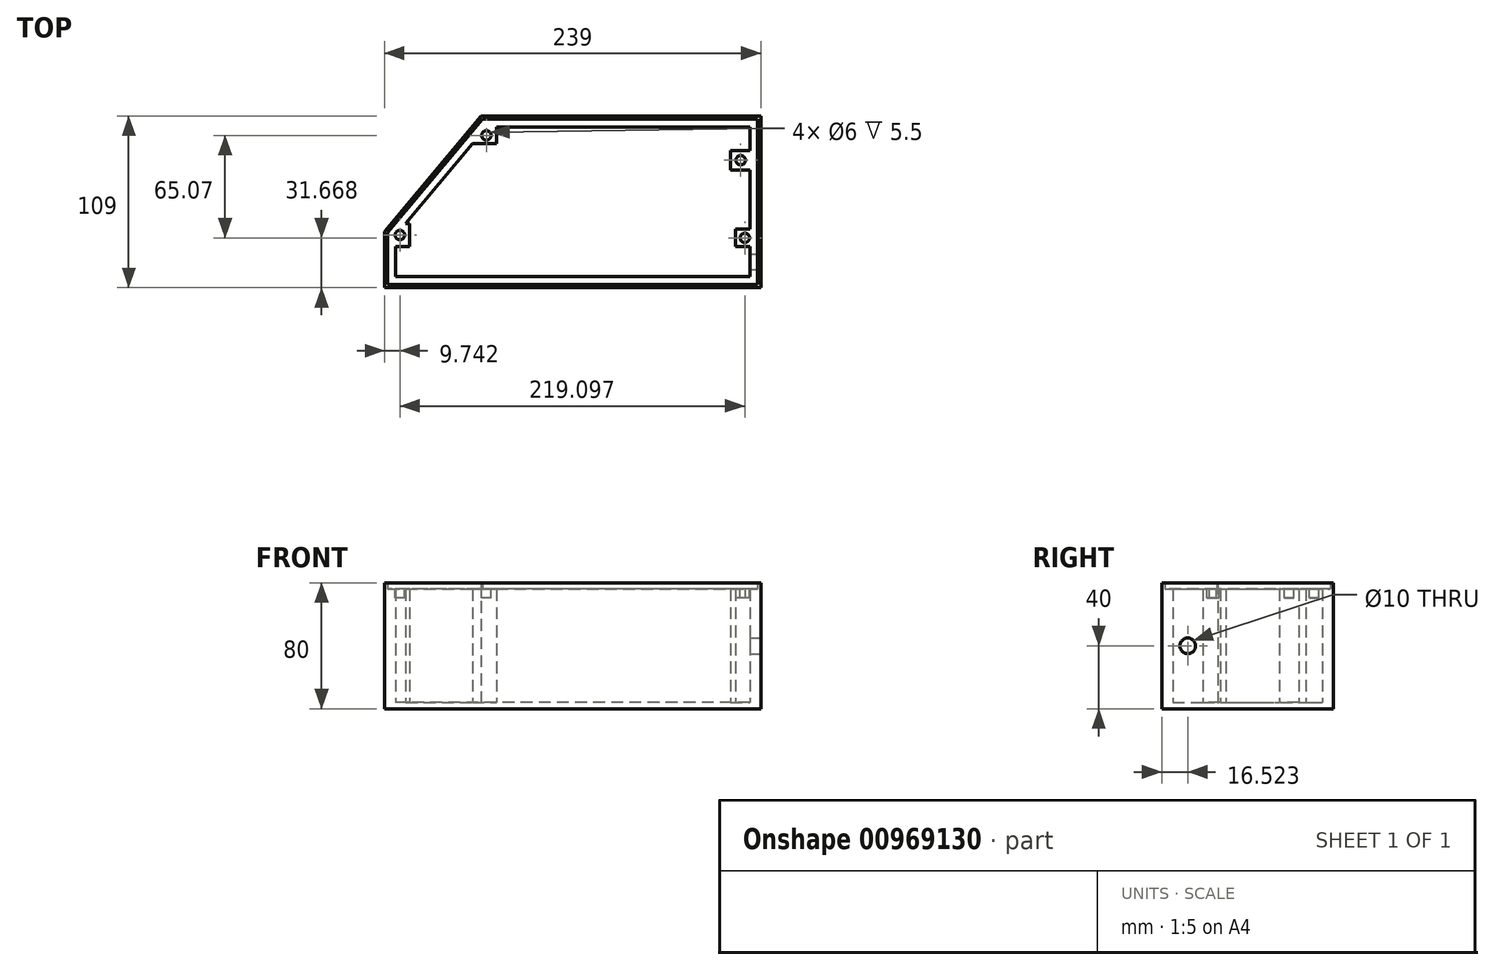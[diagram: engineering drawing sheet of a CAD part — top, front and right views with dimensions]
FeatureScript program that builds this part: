
annotation { "Feature Type Name" : "Feature", "Feature Type Description" : "" }
export const myFeature = defineFeature(function(context is Context, id is Id, definition is map)
    precondition{}
    {
        {
            var Q0;
            Q0=qCreatedBy(makeId("Top.planeOp"),FACE);
            var sketch = newSketch(context, id + "F0", { "sketchPlane" : qUnion([Q0])});
            skLineSegment(sketch, "E0", {"start": v(0, 0) * mm, "end": v(-225, 0) * mm});
            skLineSegment(sketch, "E1", {"start": v(0, 0) * mm, "end": v(0, 19.05) * mm});
            skLineSegment(sketch, "E2", {"start": v(-225, 0) * mm, "end": v(-225, 19) * mm});
            skLineSegment(sketch, "E3", {"start": v(-218.6, 33.87) * mm, "end": v(-176.22, 84.48) * mm});
            skLineSegment(sketch, "E4.0", {"start": v(0, 9) * mm, "end": v(-280, 9) * mm});
            skCircle(sketch, "E5", {"center": v(-29.7, 70.77) * mm, "radius": 9 * mm});
            skCircle(sketch, "E6.1.0.0", {"center": v(-214.7, 9) * mm, "radius": 9 * mm});
            skCircle(sketch, "E6.2.0.0", {"center": v(-196.2, 9) * mm, "radius": 9 * mm});
            skCircle(sketch, "E6.3.0.0", {"center": v(-177.7, 9) * mm, "radius": 9 * mm});
            skCircle(sketch, "E6.4.0.0", {"center": v(-159.2, 9) * mm, "radius": 9 * mm});
            skCircle(sketch, "E6.5.0.0", {"center": v(-140.7, 9) * mm, "radius": 9 * mm});
            skCircle(sketch, "E6.6.0.0", {"center": v(-122.2, 9) * mm, "radius": 9 * mm});
            skCircle(sketch, "E6.7.0.0", {"center": v(-103.7, 9) * mm, "radius": 9 * mm});
            skCircle(sketch, "E6.8.0.0", {"center": v(-85.2, 9) * mm, "radius": 9 * mm});
            skCircle(sketch, "E6.9.0.0", {"center": v(-66.7, 9) * mm, "radius": 9 * mm});
            skCircle(sketch, "E6.10.0.0", {"center": v(-48.2, 9) * mm, "radius": 9 * mm});
            skCircle(sketch, "E6.11.0.0", {"center": v(-29.7, 9) * mm, "radius": 9 * mm});
            skCircle(sketch, "E6.12.0.0", {"center": v(-11.2, 9) * mm, "radius": 9 * mm});
            skLineSegment(sketch, "E6.direction1", {"start": v(-231, 9) * mm, "end": v(-212.5, 9) * mm, "construction": true});
            skCircle(sketch, "E7", {"center": v(-186.95, 55.32) * mm, "radius": 9 * mm});
            skCircle(sketch, "E8.1.0.0", {"center": v(-205.45, 24.44) * mm, "radius": 9 * mm});
            skCircle(sketch, "E8.2.0.0", {"center": v(-186.95, 24.44) * mm, "radius": 9 * mm});
            skCircle(sketch, "E8.3.0.0", {"center": v(-168.45, 24.44) * mm, "radius": 9 * mm});
            skCircle(sketch, "E8.4.0.0", {"center": v(-149.95, 24.44) * mm, "radius": 9 * mm});
            skCircle(sketch, "E8.5.0.0", {"center": v(-131.45, 24.44) * mm, "radius": 9 * mm});
            skCircle(sketch, "E8.6.0.0", {"center": v(-112.95, 24.44) * mm, "radius": 9 * mm});
            skCircle(sketch, "E8.7.0.0", {"center": v(-94.45, 24.44) * mm, "radius": 9 * mm});
            skCircle(sketch, "E8.8.0.0", {"center": v(-75.95, 24.44) * mm, "radius": 9 * mm});
            skCircle(sketch, "E8.9.0.0", {"center": v(-57.45, 24.44) * mm, "radius": 9 * mm});
            skCircle(sketch, "E8.10.0.0", {"center": v(-38.95, 24.44) * mm, "radius": 9 * mm});
            skCircle(sketch, "E8.11.0.0", {"center": v(-20.45, 24.44) * mm, "radius": 9 * mm});
            skLineSegment(sketch, "E8.direction1", {"start": v(-221.75, 24.44) * mm, "end": v(-203.25, 24.44) * mm, "construction": true});
            skCircle(sketch, "E9", {"center": v(-196.2, 39.88) * mm, "radius": 9 * mm});
            skCircle(sketch, "E10.1.0.0", {"center": v(-177.7, 39.88) * mm, "radius": 9 * mm});
            skCircle(sketch, "E10.2.0.0", {"center": v(-159.2, 39.88) * mm, "radius": 9 * mm});
            skCircle(sketch, "E10.3.0.0", {"center": v(-140.7, 39.88) * mm, "radius": 9 * mm});
            skCircle(sketch, "E10.4.0.0", {"center": v(-122.2, 39.88) * mm, "radius": 9 * mm});
            skCircle(sketch, "E10.5.0.0", {"center": v(-103.7, 39.88) * mm, "radius": 9 * mm});
            skCircle(sketch, "E10.6.0.0", {"center": v(-85.2, 39.88) * mm, "radius": 9 * mm});
            skCircle(sketch, "E10.7.0.0", {"center": v(-66.7, 39.88) * mm, "radius": 9 * mm});
            skCircle(sketch, "E10.8.0.0", {"center": v(-48.2, 39.88) * mm, "radius": 9 * mm});
            skCircle(sketch, "E10.9.0.0", {"center": v(-29.7, 39.88) * mm, "radius": 9 * mm});
            skCircle(sketch, "E10.10.0.0", {"center": v(-11.2, 39.88) * mm, "radius": 9 * mm});
            skLineSegment(sketch, "E10.direction1", {"start": v(-194, 39.88) * mm, "end": v(-175.5, 39.88) * mm, "construction": true});
            skCircle(sketch, "E11", {"center": v(-168.45, 55.32) * mm, "radius": 9 * mm});
            skCircle(sketch, "E12.1.0.0", {"center": v(-149.95, 55.32) * mm, "radius": 9 * mm});
            skCircle(sketch, "E12.2.0.0", {"center": v(-131.45, 55.32) * mm, "radius": 9 * mm});
            skCircle(sketch, "E12.3.0.0", {"center": v(-112.95, 55.32) * mm, "radius": 9 * mm});
            skCircle(sketch, "E12.4.0.0", {"center": v(-94.45, 55.32) * mm, "radius": 9 * mm});
            skCircle(sketch, "E12.5.0.0", {"center": v(-75.95, 55.32) * mm, "radius": 9 * mm});
            skCircle(sketch, "E12.6.0.0", {"center": v(-57.45, 55.32) * mm, "radius": 9 * mm});
            skCircle(sketch, "E12.7.0.0", {"center": v(-38.95, 55.32) * mm, "radius": 9 * mm});
            skCircle(sketch, "E12.8.0.0", {"center": v(-20.45, 55.32) * mm, "radius": 9 * mm});
            skLineSegment(sketch, "E12.direction1", {"start": v(-168.45, 55.32) * mm, "end": v(-149.95, 55.32) * mm, "construction": true});
            skLineSegment(sketch, "E13.0", {"start": v(0, 95) * mm, "end": v(-160.95, 95) * mm});
            skCircle(sketch, "E14", {"center": v(-159.2, 70.77) * mm, "radius": 9 * mm});
            skCircle(sketch, "E15.1.0.0", {"center": v(-140.7, 70.77) * mm, "radius": 9 * mm});
            skCircle(sketch, "E15.2.0.0", {"center": v(-122.2, 70.77) * mm, "radius": 9 * mm});
            skCircle(sketch, "E15.3.0.0", {"center": v(-103.7, 70.77) * mm, "radius": 9 * mm});
            skCircle(sketch, "E15.4.0.0", {"center": v(-85.2, 70.77) * mm, "radius": 9 * mm});
            skCircle(sketch, "E15.5.0.0", {"center": v(-66.7, 70.77) * mm, "radius": 9 * mm});
            skCircle(sketch, "E15.6.0.0", {"center": v(-48.2, 70.77) * mm, "radius": 9 * mm});
            skLineSegment(sketch, "E15.direction1", {"start": v(-159.2, 70.77) * mm, "end": v(-140.7, 70.77) * mm, "construction": true});
            skLineSegment(sketch, "E16.0", {"start": v(-232, 28.77) * mm, "end": v(-170.67, 102) * mm});
            skLineSegment(sketch, "E16.1", {"start": v(7, 102) * mm, "end": v(-170.67, 102) * mm});
            skLineSegment(sketch, "E16.2", {"start": v(7, -7) * mm, "end": v(7, 102) * mm});
            skLineSegment(sketch, "E17.0", {"start": v(-232, -7) * mm, "end": v(-232, 28.77) * mm});
            skLineSegment(sketch, "E18.0", {"start": v(7, -7) * mm, "end": v(-232, -7) * mm});
            skLineSegment(sketch, "E19", {"start": v(-218.6, 33.87) * mm, "end": v(-216.07, 33.87) * mm});
            skLineSegment(sketch, "E20", {"start": v(-216.07, 19) * mm, "end": v(-225, 19) * mm});
            skLineSegment(sketch, "E21", {"start": v(-216.07, 19) * mm, "end": v(-216.07, 33.87) * mm});
            skLineSegment(sketch, "E22", {"start": v(0, 30.29) * mm, "end": v(-9.02, 30.29) * mm});
            skLineSegment(sketch, "E23", {"start": v(-9.02, 30.29) * mm, "end": v(-9.02, 19.05) * mm});
            skLineSegment(sketch, "E24", {"start": v(-9.02, 19.05) * mm, "end": v(0, 19.05) * mm});
            skLineSegment(sketch, "E25.trimOffspring", {"start": v(0, 30.29) * mm, "end": v(0, 67.76) * mm});
            skLineSegment(sketch, "E26", {"start": v(-176.22, 84.48) * mm, "end": v(-160.95, 84.48) * mm});
            skLineSegment(sketch, "E27", {"start": v(-160.95, 84.48) * mm, "end": v(-160.95, 95) * mm});
            skLineSegment(sketch, "E28", {"start": v(0, 80.25) * mm, "end": v(-12.43, 80.2) * mm});
            skLineSegment(sketch, "E29", {"start": v(-12.43, 80.2) * mm, "end": v(-12.38, 67.76) * mm});
            skLineSegment(sketch, "E30", {"start": v(-12.38, 67.76) * mm, "end": v(0, 67.76) * mm});
            skLineSegment(sketch, "E31.trimOffspring", {"start": v(0, 80.25) * mm, "end": v(0, 95) * mm});
            skSolve(sketch);
        }
        {
            var Q0;
            Q0 = qSketchRegion(id + "F0", true);
            extrude(context, id + "F1", {"entities" : qUnion([Q0]), "depth" : 72 * mm, "offsetDistance" : 25 * mm});
        }
        {
            var Q0;
            Q0=qCreatedBy(makeId("Top.planeOp"),FACE);
            var sketch = newSketch(context, id + "F2", { "sketchPlane" : qUnion([Q0])});
            skLineSegment(sketch, "E32.0.0", {"start": v(-232, 28.77) * mm, "end": v(-170.67, 102) * mm});
            skLineSegment(sketch, "E32.0.1", {"start": v(-170.67, 102) * mm, "end": v(7, 102) * mm});
            skLineSegment(sketch, "E32.0.2", {"start": v(7, 102) * mm, "end": v(7, -7) * mm});
            skLineSegment(sketch, "E32.0.3", {"start": v(7, -7) * mm, "end": v(-232, -7) * mm});
            skLineSegment(sketch, "E32.0.4", {"start": v(-232, -7) * mm, "end": v(-232, 28.77) * mm});
            skSolve(sketch);
        }
        {
            var Q0;
            Q0 = qSketchRegion(id + "F2", true);
            extrude(context, id + "F3", {"entities" : qUnion([Q0]), "operationType" : NewBodyOperationType.ADD, "oppositeDirection" : true, "depth" : 4 * mm, "offsetDistance" : 25 * mm});
        }
        {
            var Q0;
            Q0=makeQuery(id+"F1.opExtrude","CAP_FACE",FACE,{"disambiguationData":[OSD([sQuery(id+"F0.wireOp",EDGE,"E0"),sQuery(id+"F0.wireOp",EDGE,"E1"),sQuery(id+"F0.wireOp",EDGE,"E2"),sQuery(id+"F0.wireOp",EDGE,"E3"),sQuery(id+"F0.wireOp",EDGE,"E13.0"),sQuery(id+"F0.wireOp",EDGE,"E16.0"),sQuery(id+"F0.wireOp",EDGE,"E16.1"),sQuery(id+"F0.wireOp",EDGE,"E16.2"),sQuery(id+"F0.wireOp",EDGE,"E17.0"),sQuery(id+"F0.wireOp",EDGE,"E18.0"),sQuery(id+"F0.wireOp",EDGE,"E19"),sQuery(id+"F0.wireOp",EDGE,"E20"),sQuery(id+"F0.wireOp",EDGE,"E21"),sQuery(id+"F0.wireOp",EDGE,"E22"),sQuery(id+"F0.wireOp",EDGE,"E23"),sQuery(id+"F0.wireOp",EDGE,"E24"),sQuery(id+"F0.wireOp",EDGE,"E25.trimOffspring"),sQuery(id+"F0.wireOp",EDGE,"E26"),sQuery(id+"F0.wireOp",EDGE,"E27"),sQuery(id+"F0.wireOp",EDGE,"E28"),sQuery(id+"F0.wireOp",EDGE,"E29"),sQuery(id+"F0.wireOp",EDGE,"E30"),sQuery(id+"F0.wireOp",EDGE,"E31.trimOffspring")])],"isStart":false});
            var sketch = newSketch(context, id + "F4", { "sketchPlane" : qUnion([Q0])});
            skLineSegment(sketch, "E33.0.0", {"start": v(-170.67, 102) * mm, "end": v(-232, 28.77) * mm});
            skLineSegment(sketch, "E33.0.1", {"start": v(-232, 28.77) * mm, "end": v(-232, -7) * mm});
            skLineSegment(sketch, "E33.0.2", {"start": v(-232, -7) * mm, "end": v(7, -7) * mm});
            skLineSegment(sketch, "E33.0.3", {"start": v(7, -7) * mm, "end": v(7, 102) * mm});
            skLineSegment(sketch, "E33.0.4", {"start": v(7, 102) * mm, "end": v(-170.67, 102) * mm});
            skLineSegment(sketch, "E34.0", {"start": v(-230, 28.04) * mm, "end": v(-230, -5) * mm});
            skLineSegment(sketch, "E34.1", {"start": v(-169.74, 100) * mm, "end": v(-230, 28.04) * mm});
            skLineSegment(sketch, "E34.2", {"start": v(-230, -5) * mm, "end": v(5, -5) * mm});
            skLineSegment(sketch, "E34.3", {"start": v(5, -5) * mm, "end": v(5, 100) * mm});
            skLineSegment(sketch, "E34.4", {"start": v(5, 100) * mm, "end": v(-169.74, 100) * mm});
            skSolve(sketch);
        }
        {
            var Q0;
            Q0=makeQuery(id+"F4.imprint","IMPRINT",FACE,{"disambiguationData":[TD([[makeQuery(id+"F4.imprint","IMPRINT",EDGE,{"derivedFrom":sQuery(id+"F4.wireOp",EDGE,"E33.0.0")}),-1.0]])]});
            extrude(context, id + "F5", {"entities" : qUnion([Q0]), "operationType" : NewBodyOperationType.ADD, "depth" : 4 * mm, "offsetDistance" : 25 * mm});
        }
        {
            var Q0;
            Q0=makeQuery(id+"F5.boolean.opBoolean","MERGE",FACE,{"derivedFrom":[makeQuery(id+"F3.boolean.opBoolean","MERGE",FACE,{"derivedFrom":[makeQuery(id+"F1.opExtrude","SWEPT_FACE",FACE,{"disambiguationData":[OSD([sQuery(id+"F0.wireOp",EDGE,"E16.2")])]}),makeQuery(id+"F3.opExtrude","SWEPT_FACE",FACE,{"disambiguationData":[OSD([sQuery(id+"F2.wireOp",EDGE,"E32.0.2")])]})]}),makeQuery(id+"F5.opExtrude","SWEPT_FACE",FACE,{"disambiguationData":[OSD([sQuery(id+"F4.wireOp",EDGE,"E33.0.3")])]})]});
            var sketch = newSketch(context, id + "F6", { "sketchPlane" : qUnion([Q0])});
            skLineSegment(sketch, "E35.0.0", {"start": v(19.05, 0) * mm, "end": v(0, 0) * mm});
            skLineSegment(sketch, "E35.0.1", {"start": v(0, 0) * mm, "end": v(0, 72) * mm});
            skLineSegment(sketch, "E35.0.2", {"start": v(0, 72) * mm, "end": v(19.05, 72) * mm});
            skLineSegment(sketch, "E35.0.3", {"start": v(19.05, 72) * mm, "end": v(19.05, 0) * mm});
            skLineSegment(sketch, "E36", {"start": v(0, 36) * mm, "end": v(19.05, 36) * mm});
            skCircle(sketch, "E37", {"center": v(9.52, 36) * mm, "radius": 5 * mm});
            skSolve(sketch);
        }
        {
            var Q0;
            {var subQ0=sQuery(id+"F6.wireOp",EDGE,"E37");var subQ1=sQuery(id+"F6.wireOp",EDGE,"E36");var subQ2=makeQuery(id+"F6.imprint","INTERSECT",VERTEX,{"disambiguationData":[OD(0.0)],"derivedFrom":[subQ1,subQ0]});Q0=makeQuery(id+"F6.imprint","IMPRINT",FACE,{"disambiguationData":[TD([[makeQuery(id+"F6.imprint","IMPRINT",EDGE,{"disambiguationData":[TD([[subQ2,-1.0]])],"derivedFrom":subQ1}),1.0]])]});}
            var Q1;
            {var subQ0=sQuery(id+"F6.wireOp",EDGE,"E37");var subQ1=sQuery(id+"F6.wireOp",EDGE,"E36");var subQ2=makeQuery(id+"F6.imprint","INTERSECT",VERTEX,{"disambiguationData":[OD(0.0)],"derivedFrom":[subQ1,subQ0]});Q1=makeQuery(id+"F6.imprint","IMPRINT",FACE,{"disambiguationData":[TD([[makeQuery(id+"F6.imprint","IMPRINT",EDGE,{"disambiguationData":[TD([[subQ2,-1.0]])],"derivedFrom":subQ1}),-1.0]])]});}
            extrude(context, id + "F7", {"entities" : qUnion([Q0, Q1]), "operationType" : NewBodyOperationType.REMOVE, "oppositeDirection" : true, "depth" : 25 * mm, "offsetDistance" : 25 * mm});
        }
        {
            var Q0;
            Q0=makeQuery(id+"F1.opExtrude","CAP_FACE",FACE,{"disambiguationData":[OSD([sQuery(id+"F0.wireOp",EDGE,"E0"),sQuery(id+"F0.wireOp",EDGE,"E1"),sQuery(id+"F0.wireOp",EDGE,"E2"),sQuery(id+"F0.wireOp",EDGE,"E3"),sQuery(id+"F0.wireOp",EDGE,"E13.0"),sQuery(id+"F0.wireOp",EDGE,"E16.0"),sQuery(id+"F0.wireOp",EDGE,"E16.1"),sQuery(id+"F0.wireOp",EDGE,"E16.2"),sQuery(id+"F0.wireOp",EDGE,"E17.0"),sQuery(id+"F0.wireOp",EDGE,"E18.0"),sQuery(id+"F0.wireOp",EDGE,"E19"),sQuery(id+"F0.wireOp",EDGE,"E20"),sQuery(id+"F0.wireOp",EDGE,"E21"),sQuery(id+"F0.wireOp",EDGE,"E22"),sQuery(id+"F0.wireOp",EDGE,"E23"),sQuery(id+"F0.wireOp",EDGE,"E24"),sQuery(id+"F0.wireOp",EDGE,"E25.trimOffspring"),sQuery(id+"F0.wireOp",EDGE,"E26"),sQuery(id+"F0.wireOp",EDGE,"E27"),sQuery(id+"F0.wireOp",EDGE,"E28"),sQuery(id+"F0.wireOp",EDGE,"E29"),sQuery(id+"F0.wireOp",EDGE,"E30"),sQuery(id+"F0.wireOp",EDGE,"E31.trimOffspring")])],"isStart":false});
            var sketch = newSketch(context, id + "F8", { "sketchPlane" : qUnion([Q0])});
            skCircle(sketch, "E38", {"center": v(-167.3, 89.74) * mm, "radius": 3 * mm});
            skPoint(sketch, "E38.centerSnap0", {"position": v(-160.95, 89.74) * mm});
            skCircle(sketch, "E39", {"center": v(-222.26, 26.44) * mm, "radius": 3 * mm});
            skPoint(sketch, "E39.centerSnap0", {"position": v(-216.07, 26.44) * mm});
            skCircle(sketch, "E40", {"center": v(-5.79, 73.98) * mm, "radius": 3 * mm});
            skPoint(sketch, "E40.centerSnap0", {"position": v(-12.4, 73.98) * mm});
            skCircle(sketch, "E41", {"center": v(-3.16, 24.67) * mm, "radius": 3 * mm});
            skPoint(sketch, "E41.centerSnap0", {"position": v(-9.02, 24.67) * mm});
            skLineSegment(sketch, "E42", {"start": v(0, 0) * mm, "end": v(-27.6, 0) * mm});
            skLineSegment(sketch, "E43", {"start": v(0, 0) * mm, "end": v(0, 8.28) * mm});
            skSolve(sketch);
        }
        {
            var Q0;
            Q0 = qSketchRegion(id + "F8", true);
            extrude(context, id + "F9", {"entities" : qUnion([Q0]), "operationType" : NewBodyOperationType.REMOVE, "oppositeDirection" : true, "depth" : 5.5 * mm, "offsetDistance" : 25 * mm});
        }
    });
